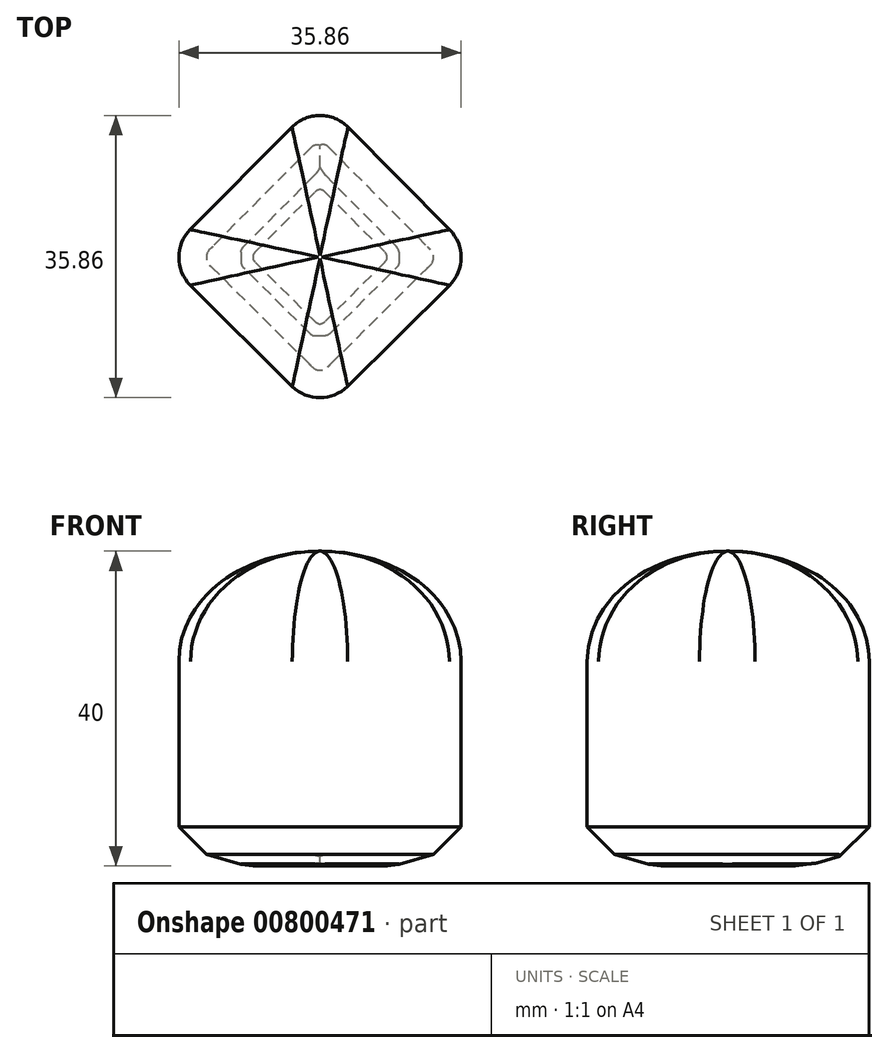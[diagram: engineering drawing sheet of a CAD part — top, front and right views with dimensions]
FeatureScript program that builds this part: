
annotation { "Feature Type Name" : "Feature", "Feature Type Description" : "" }
export const myFeature = defineFeature(function(context is Context, id is Id, definition is map)
    precondition{}
    {
        {
            var Q0;
            Q0=qCreatedBy(makeId("Top.planeOp"),FACE);
            var sketch = newSketch(context, id + "F0", { "sketchPlane" : qUnion([Q0])});
            skLineSegment(sketch, "E0", {"start": v(20, 0) * mm, "end": v(0, 20.16) * mm});
            skLineSegment(sketch, "E1", {"start": v(20, 0) * mm, "end": v(0, -19.84) * mm});
            skLineSegment(sketch, "E2.MirrorCS", {"start": v(-20, 0) * mm, "end": v(0, 20.16) * mm});
            skLineSegment(sketch, "E3.MirrorCS", {"start": v(-20, 0) * mm, "end": v(0, -19.84) * mm});
            skPoint(sketch, "E4.start.orphan", {"position": v(0, 0) * mm});
            skSolve(sketch);
        }
        {
            var Q0;
            Q0 = qSketchRegion(id + "F0", true);
            extrude(context, id + "F1", {"entities" : qUnion([Q0]), "endBound" : BoundingType.SYMMETRIC, "depth" : 40 * mm, "offsetDistance" : 25 * mm});
        }
        {
            var Q0;
            Q0=makeQuery(id+"F1.opExtrude","SWEPT_EDGE",EDGE,{"disambiguationData":[OSD([sQuery(id+"F0.wireOp",EDGE,"E0"),sQuery(id+"F0.wireOp",EDGE,"E2.MirrorCS")])]});
            var Q1;
            Q1=makeQuery(id+"F1.opExtrude","SWEPT_EDGE",EDGE,{"disambiguationData":[OSD([sQuery(id+"F0.wireOp",EDGE,"E2.MirrorCS"),sQuery(id+"F0.wireOp",EDGE,"E3.MirrorCS")])]});
            var Q2;
            Q2=makeQuery(id+"F1.opExtrude","SWEPT_EDGE",EDGE,{"disambiguationData":[OSD([sQuery(id+"F0.wireOp",EDGE,"E1"),sQuery(id+"F0.wireOp",EDGE,"E3.MirrorCS")])]});
            var Q3;
            Q3=makeQuery(id+"F1.opExtrude","SWEPT_EDGE",EDGE,{"disambiguationData":[OSD([sQuery(id+"F0.wireOp",EDGE,"E0"),sQuery(id+"F0.wireOp",EDGE,"E1")])]});
            fillet(context, id + "F2", {"entities" : qUnion([Q0, Q1, Q2, Q3]), "radius" : 5 * mm, "tangentPropagation" : true, "allowEdgeOverflow" : false});
        }
        {
            var Q0;
            Q0=makeQuery(id+"F1.opExtrude","CAP_EDGE",EDGE,{"disambiguationData":[OSD([sQuery(id+"F0.wireOp",EDGE,"E1")])],"isStart":true});
            chamfer(context, id + "F3", {"entities" : qUnion([Q0]), "width" : 5 * mm, "tangentPropagation" : true});
        }
        {
            var Q0;
            {var subQ0=sQuery(id+"F0.wireOp",EDGE,"E2.MirrorCS");Q0=makeQuery(id+"F3.opChamfer","BLEND_EDGE",EDGE,{"blendedFrom":[makeQuery(id+"F1.opExtrude","CAP_EDGE",EDGE,{"disambiguationData":[OSD([subQ0])],"isStart":true}),makeQuery(id+"F1.opExtrude","CAP_FACE",FACE,{"disambiguationData":[OSD([sQuery(id+"F0.wireOp",EDGE,"E0"),sQuery(id+"F0.wireOp",EDGE,"E1"),subQ0,sQuery(id+"F0.wireOp",EDGE,"E3.MirrorCS")])],"isStart":true})],"blendedInto":[makeQuery(id+"F1.opExtrude","CAP_FACE",FACE,{"disambiguationData":[OSD([sQuery(id+"F0.wireOp",EDGE,"E0"),sQuery(id+"F0.wireOp",EDGE,"E1"),subQ0,sQuery(id+"F0.wireOp",EDGE,"E3.MirrorCS")])],"isStart":true})]});}
            chamfer(context, id + "F4", {"entities" : qUnion([Q0]), "width" : 5 * mm, "tangentPropagation" : true});
        }
        {
            var Q0;
            {var subQ0=sQuery(id+"F0.wireOp",EDGE,"E2.MirrorCS");var subQ1=makeQuery(id+"F1.opExtrude","CAP_FACE",FACE,{"disambiguationData":[OSD([sQuery(id+"F0.wireOp",EDGE,"E0"),sQuery(id+"F0.wireOp",EDGE,"E1"),subQ0,sQuery(id+"F0.wireOp",EDGE,"E3.MirrorCS")])],"isStart":true});Q0=makeQuery(id+"F4.opChamfer","BLEND_EDGE",EDGE,{"blendedFrom":[makeQuery(id+"F3.opChamfer","BLEND_EDGE",EDGE,{"blendedFrom":[makeQuery(id+"F1.opExtrude","CAP_EDGE",EDGE,{"disambiguationData":[OSD([subQ0])],"isStart":true}),subQ1],"blendedInto":[subQ1]}),subQ1],"blendedInto":[subQ1]});}
            var Q1;
            {var subQ0=sQuery(id+"F0.wireOp",EDGE,"E3.MirrorCS");var subQ1=makeQuery(id+"F1.opExtrude","CAP_FACE",FACE,{"disambiguationData":[OSD([sQuery(id+"F0.wireOp",EDGE,"E0"),sQuery(id+"F0.wireOp",EDGE,"E1"),sQuery(id+"F0.wireOp",EDGE,"E2.MirrorCS"),subQ0])],"isStart":true});Q1=makeQuery(id+"F4.opChamfer","BLEND_EDGE",EDGE,{"blendedFrom":[makeQuery(id+"F3.opChamfer","BLEND_EDGE",EDGE,{"blendedFrom":[makeQuery(id+"F1.opExtrude","CAP_EDGE",EDGE,{"disambiguationData":[OSD([subQ0])],"isStart":true}),subQ1],"blendedInto":[subQ1]}),subQ1],"blendedInto":[subQ1]});}
            var Q2;
            {var subQ0=sQuery(id+"F0.wireOp",EDGE,"E1");var subQ1=makeQuery(id+"F1.opExtrude","CAP_FACE",FACE,{"disambiguationData":[OSD([sQuery(id+"F0.wireOp",EDGE,"E0"),subQ0,sQuery(id+"F0.wireOp",EDGE,"E2.MirrorCS"),sQuery(id+"F0.wireOp",EDGE,"E3.MirrorCS")])],"isStart":true});Q2=makeQuery(id+"F4.opChamfer","BLEND_EDGE",EDGE,{"blendedFrom":[makeQuery(id+"F3.opChamfer","BLEND_EDGE",EDGE,{"blendedFrom":[makeQuery(id+"F1.opExtrude","CAP_EDGE",EDGE,{"disambiguationData":[OSD([subQ0])],"isStart":true}),subQ1],"blendedInto":[subQ1]}),subQ1],"blendedInto":[subQ1]});}
            var Q3;
            {var subQ0=sQuery(id+"F0.wireOp",EDGE,"E0");var subQ1=makeQuery(id+"F1.opExtrude","CAP_FACE",FACE,{"disambiguationData":[OSD([subQ0,sQuery(id+"F0.wireOp",EDGE,"E1"),sQuery(id+"F0.wireOp",EDGE,"E2.MirrorCS"),sQuery(id+"F0.wireOp",EDGE,"E3.MirrorCS")])],"isStart":true});Q3=makeQuery(id+"F4.opChamfer","BLEND_EDGE",EDGE,{"blendedFrom":[makeQuery(id+"F3.opChamfer","BLEND_EDGE",EDGE,{"blendedFrom":[makeQuery(id+"F1.opExtrude","CAP_EDGE",EDGE,{"disambiguationData":[OSD([subQ0])],"isStart":true}),subQ1],"blendedInto":[subQ1]}),subQ1],"blendedInto":[subQ1]});}
            chamfer(context, id + "F5", {"entities" : qUnion([Q0, Q1, Q2, Q3]), "width" : 4 * mm, "tangentPropagation" : true});
        }
        {
            var Q0;
            {var subQ0=sQuery(id+"F0.wireOp",EDGE,"E2.MirrorCS");var subQ1=sQuery(id+"F0.wireOp",EDGE,"E0");var subQ2=makeQuery(id+"F1.opExtrude","CAP_FACE",FACE,{"disambiguationData":[OSD([subQ1,sQuery(id+"F0.wireOp",EDGE,"E1"),subQ0,sQuery(id+"F0.wireOp",EDGE,"E3.MirrorCS")])],"isStart":true});var subQ3=subQ2;Q0=makeQuery(id+"F5.opChamfer","BLEND_EDGE",EDGE,{"blendedFrom":[makeQuery(id+"F4.opChamfer","BLEND_EDGE",EDGE,{"blendedFrom":[makeQuery(id+"F3.opChamfer","BLEND_EDGE",EDGE,{"blendedFrom":[makeQuery(id+"F1.opExtrude","CAP_EDGE",EDGE,{"disambiguationData":[OSD([subQ1])],"isStart":true}),subQ2],"blendedInto":[subQ2]}),subQ3],"blendedInto":[subQ3]}),makeQuery(id+"F4.opChamfer","BLEND_EDGE",EDGE,{"blendedFrom":[makeQuery(id+"F3.opChamfer","BLEND_EDGE",EDGE,{"blendedFrom":[makeQuery(id+"F1.opExtrude","CAP_EDGE",EDGE,{"disambiguationData":[OSD([subQ0])],"isStart":true}),subQ2],"blendedInto":[subQ2]}),subQ3],"blendedInto":[subQ3]})],"blendedInto":[]});}
            var Q1;
            {var subQ0=sQuery(id+"F0.wireOp",EDGE,"E3.MirrorCS");var subQ1=sQuery(id+"F0.wireOp",EDGE,"E1");var subQ2=makeQuery(id+"F1.opExtrude","CAP_FACE",FACE,{"disambiguationData":[OSD([sQuery(id+"F0.wireOp",EDGE,"E0"),subQ1,sQuery(id+"F0.wireOp",EDGE,"E2.MirrorCS"),subQ0])],"isStart":true});var subQ3=subQ2;Q1=makeQuery(id+"F5.opChamfer","BLEND_EDGE",EDGE,{"blendedFrom":[makeQuery(id+"F4.opChamfer","BLEND_EDGE",EDGE,{"blendedFrom":[makeQuery(id+"F3.opChamfer","BLEND_EDGE",EDGE,{"blendedFrom":[makeQuery(id+"F1.opExtrude","CAP_EDGE",EDGE,{"disambiguationData":[OSD([subQ1])],"isStart":true}),subQ2],"blendedInto":[subQ2]}),subQ3],"blendedInto":[subQ3]}),makeQuery(id+"F4.opChamfer","BLEND_EDGE",EDGE,{"blendedFrom":[makeQuery(id+"F3.opChamfer","BLEND_EDGE",EDGE,{"blendedFrom":[makeQuery(id+"F1.opExtrude","CAP_EDGE",EDGE,{"disambiguationData":[OSD([subQ0])],"isStart":true}),subQ2],"blendedInto":[subQ2]}),subQ3],"blendedInto":[subQ3]})],"blendedInto":[]});}
            var Q2;
            {var subQ0=sQuery(id+"F0.wireOp",EDGE,"E3.MirrorCS");var subQ1=sQuery(id+"F0.wireOp",EDGE,"E2.MirrorCS");var subQ2=makeQuery(id+"F1.opExtrude","CAP_FACE",FACE,{"disambiguationData":[OSD([sQuery(id+"F0.wireOp",EDGE,"E0"),sQuery(id+"F0.wireOp",EDGE,"E1"),subQ1,subQ0])],"isStart":true});var subQ3=subQ2;Q2=makeQuery(id+"F5.opChamfer","BLEND_EDGE",EDGE,{"blendedFrom":[makeQuery(id+"F4.opChamfer","BLEND_EDGE",EDGE,{"blendedFrom":[makeQuery(id+"F3.opChamfer","BLEND_EDGE",EDGE,{"blendedFrom":[makeQuery(id+"F1.opExtrude","CAP_EDGE",EDGE,{"disambiguationData":[OSD([subQ1])],"isStart":true}),subQ2],"blendedInto":[subQ2]}),subQ3],"blendedInto":[subQ3]}),makeQuery(id+"F4.opChamfer","BLEND_EDGE",EDGE,{"blendedFrom":[makeQuery(id+"F3.opChamfer","BLEND_EDGE",EDGE,{"blendedFrom":[makeQuery(id+"F1.opExtrude","CAP_EDGE",EDGE,{"disambiguationData":[OSD([subQ0])],"isStart":true}),subQ2],"blendedInto":[subQ2]}),subQ3],"blendedInto":[subQ3]})],"blendedInto":[]});}
            var Q3;
            {var subQ0=sQuery(id+"F0.wireOp",EDGE,"E1");var subQ1=sQuery(id+"F0.wireOp",EDGE,"E0");var subQ2=makeQuery(id+"F1.opExtrude","CAP_FACE",FACE,{"disambiguationData":[OSD([subQ1,subQ0,sQuery(id+"F0.wireOp",EDGE,"E2.MirrorCS"),sQuery(id+"F0.wireOp",EDGE,"E3.MirrorCS")])],"isStart":true});var subQ3=subQ2;Q3=makeQuery(id+"F5.opChamfer","BLEND_EDGE",EDGE,{"blendedFrom":[makeQuery(id+"F4.opChamfer","BLEND_EDGE",EDGE,{"blendedFrom":[makeQuery(id+"F3.opChamfer","BLEND_EDGE",EDGE,{"blendedFrom":[makeQuery(id+"F1.opExtrude","CAP_EDGE",EDGE,{"disambiguationData":[OSD([subQ1])],"isStart":true}),subQ2],"blendedInto":[subQ2]}),subQ3],"blendedInto":[subQ3]}),makeQuery(id+"F4.opChamfer","BLEND_EDGE",EDGE,{"blendedFrom":[makeQuery(id+"F3.opChamfer","BLEND_EDGE",EDGE,{"blendedFrom":[makeQuery(id+"F1.opExtrude","CAP_EDGE",EDGE,{"disambiguationData":[OSD([subQ0])],"isStart":true}),subQ2],"blendedInto":[subQ2]}),subQ3],"blendedInto":[subQ3]})],"blendedInto":[]});}
            var Q4;
            {var subQ0=sQuery(id+"F0.wireOp",EDGE,"E3.MirrorCS");var subQ1=sQuery(id+"F0.wireOp",EDGE,"E2.MirrorCS");var subQ2=makeQuery(id+"F1.opExtrude","CAP_FACE",FACE,{"disambiguationData":[OSD([sQuery(id+"F0.wireOp",EDGE,"E0"),sQuery(id+"F0.wireOp",EDGE,"E1"),subQ1,subQ0])],"isStart":true});Q4=makeQuery(id+"F4.opChamfer","BLEND_EDGE",EDGE,{"blendedFrom":[makeQuery(id+"F3.opChamfer","BLEND_EDGE",EDGE,{"blendedFrom":[makeQuery(id+"F1.opExtrude","CAP_EDGE",EDGE,{"disambiguationData":[OSD([subQ1])],"isStart":true}),subQ2],"blendedInto":[subQ2]}),makeQuery(id+"F3.opChamfer","BLEND_EDGE",EDGE,{"blendedFrom":[makeQuery(id+"F1.opExtrude","CAP_EDGE",EDGE,{"disambiguationData":[OSD([subQ0])],"isStart":true}),subQ2],"blendedInto":[subQ2]})],"blendedInto":[]});}
            var Q5;
            {var subQ0=sQuery(id+"F0.wireOp",EDGE,"E3.MirrorCS");var subQ1=sQuery(id+"F0.wireOp",EDGE,"E1");var subQ2=makeQuery(id+"F1.opExtrude","CAP_FACE",FACE,{"disambiguationData":[OSD([sQuery(id+"F0.wireOp",EDGE,"E0"),subQ1,sQuery(id+"F0.wireOp",EDGE,"E2.MirrorCS"),subQ0])],"isStart":true});Q5=makeQuery(id+"F4.opChamfer","BLEND_EDGE",EDGE,{"blendedFrom":[makeQuery(id+"F3.opChamfer","BLEND_EDGE",EDGE,{"blendedFrom":[makeQuery(id+"F1.opExtrude","CAP_EDGE",EDGE,{"disambiguationData":[OSD([subQ1])],"isStart":true}),subQ2],"blendedInto":[subQ2]}),makeQuery(id+"F3.opChamfer","BLEND_EDGE",EDGE,{"blendedFrom":[makeQuery(id+"F1.opExtrude","CAP_EDGE",EDGE,{"disambiguationData":[OSD([subQ0])],"isStart":true}),subQ2],"blendedInto":[subQ2]})],"blendedInto":[]});}
            var Q6;
            {var subQ0=sQuery(id+"F0.wireOp",EDGE,"E1");var subQ1=sQuery(id+"F0.wireOp",EDGE,"E0");var subQ2=makeQuery(id+"F1.opExtrude","CAP_FACE",FACE,{"disambiguationData":[OSD([subQ1,subQ0,sQuery(id+"F0.wireOp",EDGE,"E2.MirrorCS"),sQuery(id+"F0.wireOp",EDGE,"E3.MirrorCS")])],"isStart":true});Q6=makeQuery(id+"F4.opChamfer","BLEND_EDGE",EDGE,{"blendedFrom":[makeQuery(id+"F3.opChamfer","BLEND_EDGE",EDGE,{"blendedFrom":[makeQuery(id+"F1.opExtrude","CAP_EDGE",EDGE,{"disambiguationData":[OSD([subQ1])],"isStart":true}),subQ2],"blendedInto":[subQ2]}),makeQuery(id+"F3.opChamfer","BLEND_EDGE",EDGE,{"blendedFrom":[makeQuery(id+"F1.opExtrude","CAP_EDGE",EDGE,{"disambiguationData":[OSD([subQ0])],"isStart":true}),subQ2],"blendedInto":[subQ2]})],"blendedInto":[]});}
            fillet(context, id + "F6", {"entities" : qUnion([Q0, Q1, Q2, Q3, Q4, Q5, Q6]), "radius" : 5 * mm, "tangentPropagation" : true, "allowEdgeOverflow" : false});
        }
        {
            var Q0;
            {var subQ0=sQuery(id+"F0.wireOp",EDGE,"E2.MirrorCS");var subQ1=sQuery(id+"F0.wireOp",EDGE,"E0");Q0=makeQuery(id+"F2.opFillet","BLEND_EDGE",EDGE,{"blendedFrom":[makeQuery(id+"F1.opExtrude","SWEPT_EDGE",EDGE,{"disambiguationData":[OSD([subQ1,subQ0])]}),makeQuery(id+"F1.opExtrude","CAP_FACE",FACE,{"disambiguationData":[OSD([subQ1,sQuery(id+"F0.wireOp",EDGE,"E1"),subQ0,sQuery(id+"F0.wireOp",EDGE,"E3.MirrorCS")])],"isStart":false})],"blendedInto":[makeQuery(id+"F1.opExtrude","CAP_FACE",FACE,{"disambiguationData":[OSD([subQ1,sQuery(id+"F0.wireOp",EDGE,"E1"),subQ0,sQuery(id+"F0.wireOp",EDGE,"E3.MirrorCS")])],"isStart":false})]});}
            fillet(context, id + "F7", {"entities" : qUnion([Q0]), "radius" : 14 * mm, "tangentPropagation" : true, "allowEdgeOverflow" : false});
        }
    });
